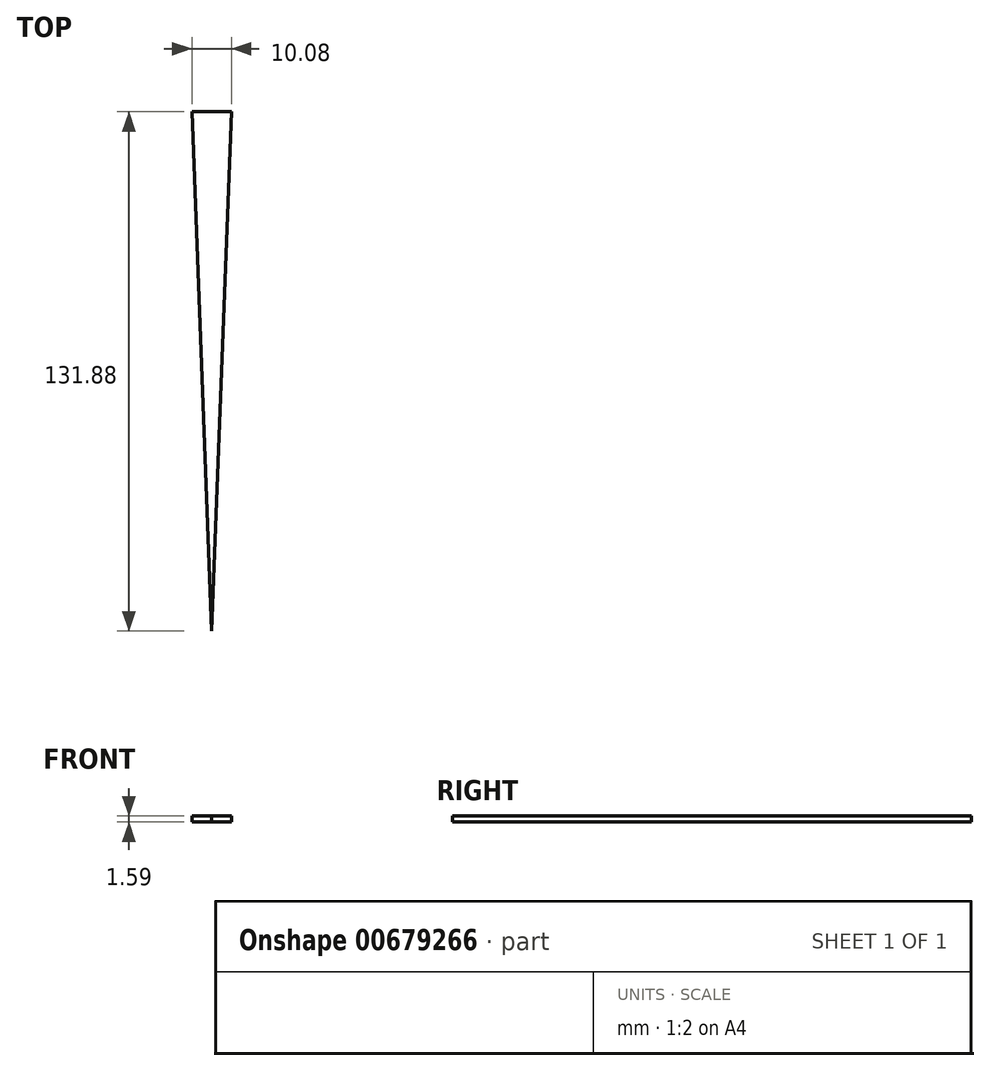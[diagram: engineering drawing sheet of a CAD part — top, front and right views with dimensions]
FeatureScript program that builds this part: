
annotation { "Feature Type Name" : "Feature", "Feature Type Description" : "" }
export const myFeature = defineFeature(function(context is Context, id is Id, definition is map)
    precondition{}
    {
        {
            var Q0;
            Q0=qCreatedBy(makeId("Top.planeOp"),FACE);
            var sketch = newSketch(context, id + "F0", { "sketchPlane" : qUnion([Q0])});
            skLineSegment(sketch, "E0.bottom", {"start": v(5.04, 65.94) * mm, "end": v(-5.04, 65.94) * mm});
            skPoint(sketch, "E0.middle", {"position": v(0, 0) * mm});
            skLineSegment(sketch, "E1", {"start": v(-5.04, 65.94) * mm, "end": v(0, -65.94) * mm});
            skLineSegment(sketch, "E2", {"start": v(0, -65.94) * mm, "end": v(5.04, 65.94) * mm});
            skPoint(sketch, "E0.left.end.orphan", {"position": v(5.04, -65.94) * mm});
            skPoint(sketch, "E0.right.end.orphan", {"position": v(-5.04, -65.94) * mm});
            skLineSegment(sketch, "E3", {"start": v(0, 65.94) * mm, "end": v(0, -65.94) * mm});
            skSolve(sketch);
        }
        {
            var Q0;
            Q0=qSketchRegion(id+"F0",true);
            extrude(context, id + "F1", {"entities" : qUnion([Q0]), "depth" : 1.59 * mm});
        }
    });
